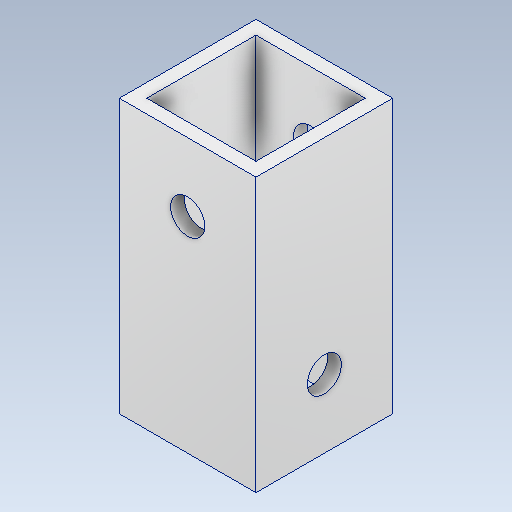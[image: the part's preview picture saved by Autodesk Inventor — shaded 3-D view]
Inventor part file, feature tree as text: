
AUTODESK INVENTOR PART (.ipt)
format: ipt  version: 2020.3 (Build 243373000, 373)  size: 140,288 bytes
history: native  units: mm
features: sketch x3, hole x2, other x1, extrude x1
ambient origin geometry x8: Origin, YZ Plane, XZ Plane, XY Plane, X Axis, Y Axis, Z Axis, Center Point
bodies: Body1 (feature_tree)
feature tree (7):
  other  "ソリッド1"
  extrude  "押し出し1"  Depth=12.0mm
  hole  "穴1"  [1 undecoded]
  hole  "穴2"  [1 undecoded]
  sketch  "スケッチ1"
  sketch  "スケッチ2"
  sketch  "スケッチ3"
note: 2 required parameter values undecoded (feature->parameter linkage not recoverable at this tier; creation-order binding heuristic only, values carry confidence <= 0.55)
